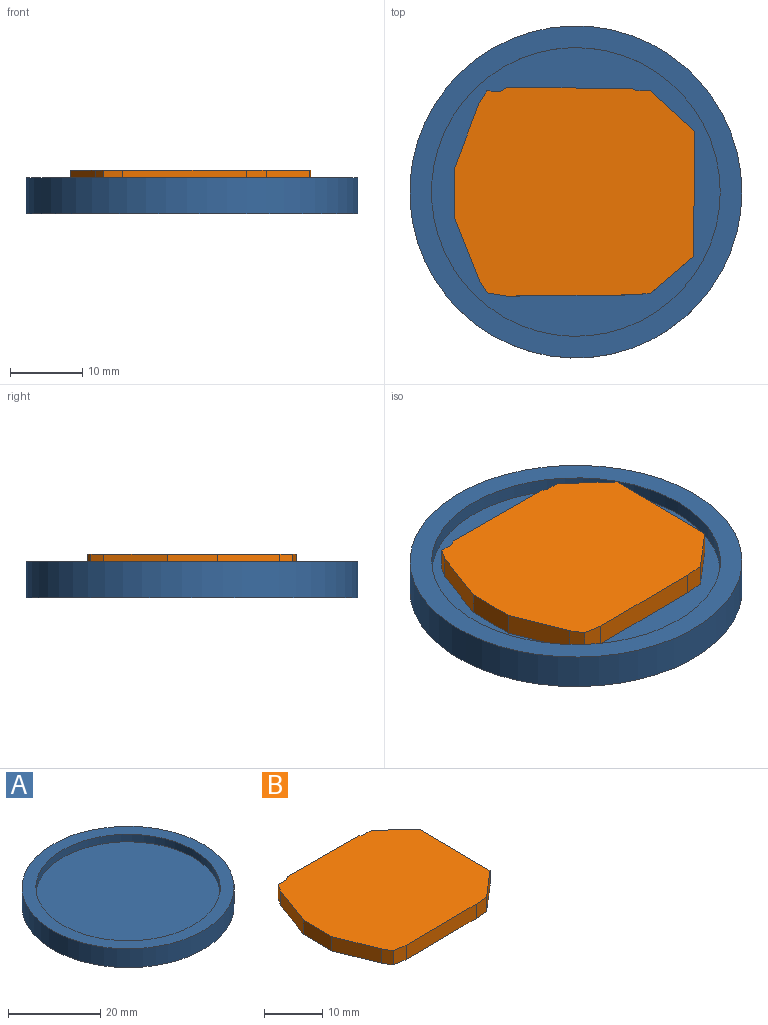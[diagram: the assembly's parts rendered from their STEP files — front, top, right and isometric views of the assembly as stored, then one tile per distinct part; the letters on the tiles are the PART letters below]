
ASSEMBLY  parts=2 mates=1
PART A: 5 faces, bbox 46x46x5 mm
  f0: plane 40x40mm, normal (0,0,1), area 1256.6mm2, adj f1
  f1: cylinder r=20mm len=40mm, axis (0,0,-1), area 251.3mm2, adj f0,f3
  f2: cylinder r=23mm len=46mm, axis (0,0,-1), area 722.6mm2, adj f3,f4
  f3: plane 46x46mm, normal (0,0,1), area 405.3mm2, adj f1,f2
  f4: plane 46x46mm, normal (0,0,-1), area 1661.9mm2, adj f2
PART B: 18 faces, bbox 33.3x28.9x3 mm
  f0: plane 3x1.92mm, normal (0.02,1,0), area 5.8mm2, adj f1,f15,f16,f17
  f1: plane 3x1.75mm, normal (-0.85,0.53,0), area 6.2mm2, adj f0,f2,f16,f17
  f2: plane 8.85x3.3mm, normal (-0.94,0.35,0), area 28.3mm2, adj f1,f3,f16,f17
  f3: plane 6.93x3mm, normal (-1,0.01,0), area 20.8mm2, adj f2,f4,f16,f17
  f4: plane 8.64x3.43mm, normal (-0.93,-0.37,0), area 27.9mm2, adj f3,f5,f16,f17
  f5: plane 3x1.79mm, normal (-0.85,-0.52,0), area 6.3mm2, adj f4,f6,f16,f17
  f6: plane 3x2.69mm, normal (-0.16,-0.99,0), area 8.2mm2, adj f5,f7,f16,f17
  f7: plane 17.17x3mm, normal (0.01,-1,0), area 51.5mm2, adj f6,f8,f16,f17
  f8: plane 3x2.73mm, normal (0.07,-1,0), area 8.2mm2, adj f7,f9,f16,f17
  f9: plane 5.99x5.14mm, normal (0.65,-0.76,0), area 23.7mm2, adj f8,f10,f16,f17
  f10: plane 17.33x3mm, normal (1,-0.01,0), area 52mm2, adj f9,f11,f16,f17
  f11: plane 6.16x5.59mm, normal (0.67,0.74,0), area 24.9mm2, adj f10,f12,f16,f17
  f12: plane 3x1.88mm, normal (0.02,1,0), area 5.6mm2, adj f11,f13,f16,f17
  f13: plane 3x0.77mm, normal (0.39,0.92,0), area 2.5mm2, adj f12,f14,f16,f17
  f14: plane 17.25x3mm, normal (0,1,0), area 51.7mm2, adj f13,f15,f16,f17
  f15: plane 3x0.86mm, normal (-0.5,0.87,0), area 3mm2, adj f0,f14,f16,f17
  f16: plane 33.31x28.87mm, normal (0,0,1), area 867.2mm2, adj f0,f1,f2,f3,f4,f5,f6,f7
  f17: plane 33.31x28.87mm, normal (0,0,-1), area 867.2mm2, adj f0,f1,f2,f3,f4,f5,f6,f7
PLACE A t=(0.17,-0.01,12.8)mm
PLACE B t=(0,0,15.8)mm
MATE planar A.f1 <-> B.f17  axis (0,0,1) through (0.17,-0.01,15.8)mm
